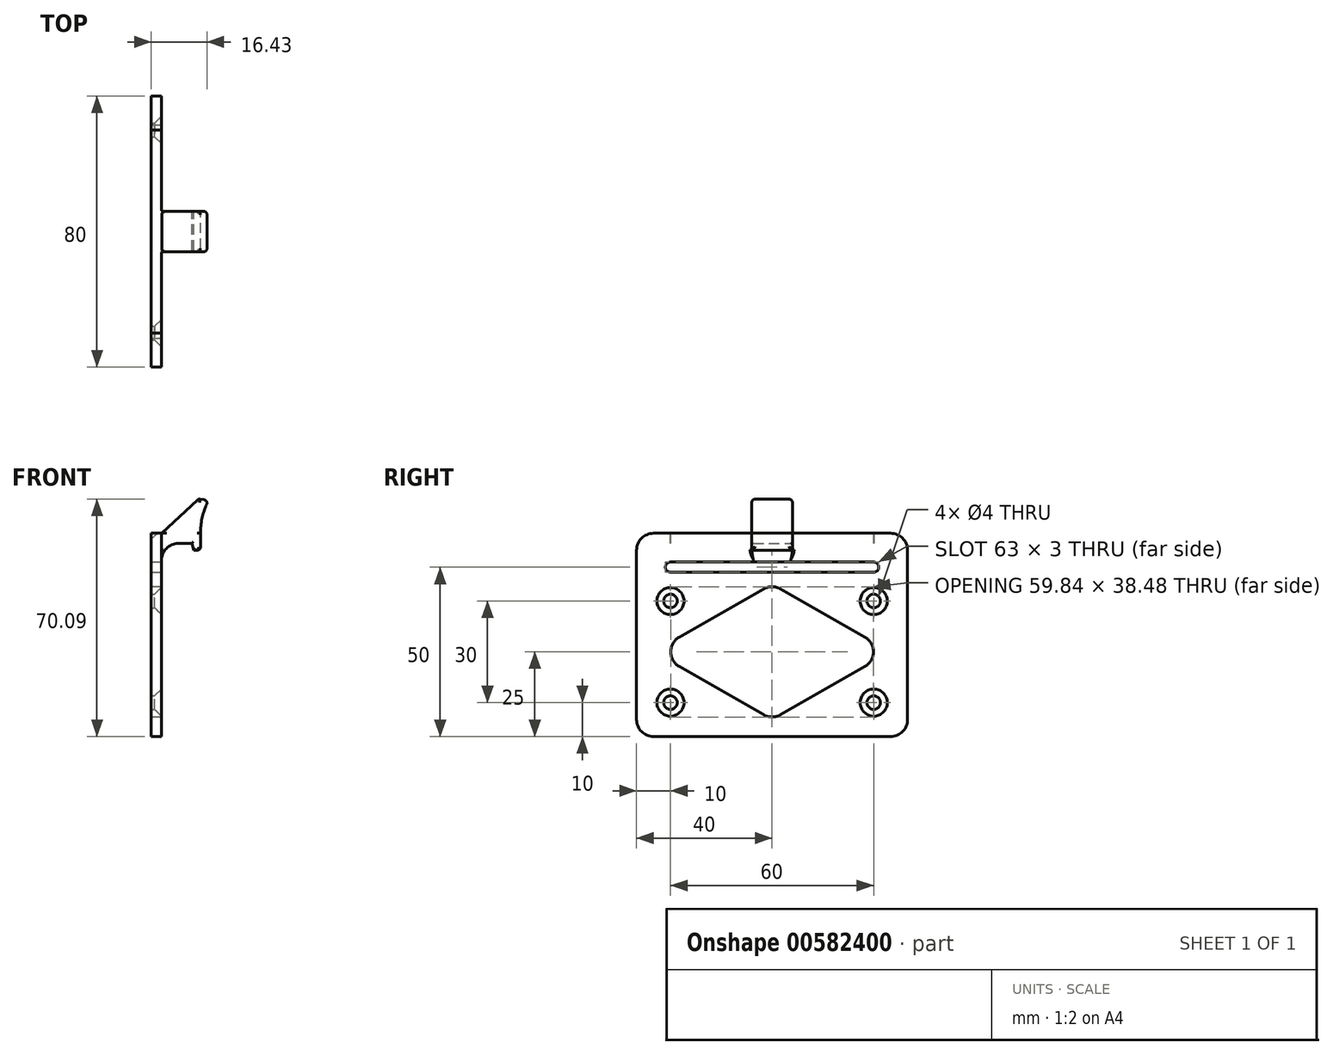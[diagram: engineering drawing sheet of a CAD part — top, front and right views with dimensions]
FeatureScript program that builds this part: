
annotation { "Feature Type Name" : "Feature", "Feature Type Description" : "" }
export const myFeature = defineFeature(function(context is Context, id is Id, definition is map)
    precondition{}
    {
        {
            var Q0;
            Q0=qCreatedBy(makeId("Front.planeOp"),FACE);
            var sketch = newSketch(context, id + "F0", { "sketchPlane" : qUnion([Q0])});
            skLineSegment(sketch, "E0.bottom", {"start": v(0, 0) * mm, "end": v(3, 0) * mm});
            skLineSegment(sketch, "E0.top", {"start": v(0, 60) * mm, "end": v(14.54, 60) * mm});
            skLineSegment(sketch, "E0.left", {"start": v(0, 0) * mm, "end": v(0, 60) * mm});
            skLineSegment(sketch, "E0.right", {"start": v(14.54, 55) * mm, "end": v(14.54, 60) * mm});
            skLineSegment(sketch, "E1", {"start": v(14.54, 55) * mm, "end": v(12.54, 55) * mm});
            skLineSegment(sketch, "E2", {"start": v(3, 52) * mm, "end": v(3, 0) * mm});
            skLineSegment(sketch, "E3", {"start": v(8, 57) * mm, "end": v(12, 57) * mm});
            skPoint(sketch, "E4.newPointA", {"position": v(3, 55) * mm});
            skArc(sketch, "E4.filletArc", {"start": v(8, 57) * mm, "mid": v(4.46, 55.54) * mm, "end": v(3, 52) * mm});
            skLineSegment(sketch, "E5", {"start": v(12, 57) * mm, "end": v(12.54, 55) * mm});
            skPoint(sketch, "E6.orphan", {"position": v(10.1, 55) * mm});
            skSolve(sketch);
        }
        {
            var Q0;
            Q0=makeQuery(id+"F0.imprint","IMPRINT",FACE,{"disambiguationData":[TD([[makeQuery(id+"F0.imprint","IMPRINT",EDGE,{"derivedFrom":sQuery(id+"F0.wireOp",EDGE,"E0.bottom")}),1.0]])]});
            extrude(context, id + "F1", {"entities" : qUnion([Q0]), "endBound" : BoundingType.SYMMETRIC, "depth" : 80 * mm, "offsetDistance" : 25 * mm});
        }
        {
            var Q0;
            Q0=makeQuery(id+"F1.opExtrude","SWEPT_FACE",FACE,{"disambiguationData":[OSD([sQuery(id+"F0.wireOp",EDGE,"E0.top")])]});
            var sketch = newSketch(context, id + "F2", { "sketchPlane" : qUnion([Q0])});
            skLineSegment(sketch, "E7", {"start": v(3, -40) * mm, "end": v(3, -6) * mm});
            skLineSegment(sketch, "E8", {"start": v(3, -6) * mm, "end": v(14.54, -6) * mm});
            skLineSegment(sketch, "E9.MirrorCS", {"start": v(3, 6) * mm, "end": v(14.54, 6) * mm});
            skLineSegment(sketch, "E10.MirrorCS", {"start": v(3, 40) * mm, "end": v(3, 6) * mm});
            skSolve(sketch);
        }
        {
            var Q0;
            {var subQ0=sQuery(id+"F2.wireOp",EDGE,"E7");Q0=makeQuery(id+"F2.imprint","IMPRINT",FACE,{"disambiguationData":[TD([[makeQuery(id+"F2.imprint","IMPRINT",EDGE,{"derivedFrom":subQ0}),-1.0]])]});}
            var Q1;
            {var subQ0=sQuery(id+"F2.wireOp",EDGE,"E9.MirrorCS");Q1=makeQuery(id+"F2.imprint","IMPRINT",FACE,{"disambiguationData":[TD([[makeQuery(id+"F2.imprint","IMPRINT",EDGE,{"derivedFrom":subQ0}),1.0]])]});}
            extrude(context, id + "F3", {"entities" : qUnion([Q0, Q1]), "operationType" : NewBodyOperationType.REMOVE, "endBound" : BoundingType.THROUGH_ALL, "oppositeDirection" : true, "depth" : 25 * mm, "offsetDistance" : 25 * mm});
        }
        {
            var Q0;
            Q0=makeQuery(id+"F3.boolean.opBoolean","MERGE",FACE,{"derivedFrom":[makeQuery(id+"F1.opExtrude","SWEPT_FACE",FACE,{"disambiguationData":[OSD([sQuery(id+"F0.wireOp",EDGE,"E2")])]}),makeQuery(id+"F3.opExtrude","SWEPT_FACE",FACE,{"disambiguationData":[OSD([sQuery(id+"F2.wireOp",EDGE,"E7")])]}),makeQuery(id+"F3.opExtrude","SWEPT_FACE",FACE,{"disambiguationData":[OSD([sQuery(id+"F2.wireOp",EDGE,"E10.MirrorCS")])]})]});
            var sketch = newSketch(context, id + "F4", { "sketchPlane" : qUnion([Q0])});
            skLineSegment(sketch, "E11.bottom", {"start": v(-30, 51.5) * mm, "end": v(30, 51.5) * mm});
            skLineSegment(sketch, "E11.top", {"start": v(-30, 48.5) * mm, "end": v(30, 48.5) * mm});
            skArc(sketch, "E12", {"start": v(30, 48.5) * mm, "mid": v(31.5, 50) * mm, "end": v(30, 51.5) * mm});
            skArc(sketch, "E13", {"start": v(-30, 51.5) * mm, "mid": v(-31.5, 50) * mm, "end": v(-30, 48.5) * mm});
            skSolve(sketch);
        }
        {
            var Q0;
            Q0=makeQuery(id+"F4.imprint","IMPRINT",FACE,{"disambiguationData":[TD([[makeQuery(id+"F4.imprint","IMPRINT",EDGE,{"derivedFrom":sQuery(id+"F4.wireOp",EDGE,"E11.bottom")}),-1.0]])]});
            extrude(context, id + "F5", {"entities" : qUnion([Q0]), "operationType" : NewBodyOperationType.REMOVE, "endBound" : BoundingType.THROUGH_ALL, "oppositeDirection" : true, "depth" : 25 * mm, "offsetDistance" : 25 * mm});
        }
        {
            var Q0;
            Q0=qCreatedBy(makeId("Front.planeOp"),FACE);
            var sketch = newSketch(context, id + "F6", { "sketchPlane" : qUnion([Q0])});
            skArc(sketch, "E14", {"start": v(3, 60) * mm, "mid": v(0.88, 59.12) * mm, "end": v(0, 57) * mm});
            skLineSegment(sketch, "E15", {"start": v(0, 57) * mm, "end": v(0, 60) * mm});
            skLineSegment(sketch, "E16", {"start": v(0, 60) * mm, "end": v(3, 60) * mm});
            skSolve(sketch);
        }
        {
            var Q0;
            Q0 = qSketchRegion(id + "F6", true);
            extrude(context, id + "F7", {"entities" : qUnion([Q0]), "operationType" : NewBodyOperationType.REMOVE, "endBound" : BoundingType.SYMMETRIC, "depth" : 60 * mm, "offsetDistance" : 25 * mm});
        }
        {
            var Q0;
            Q0=qCreatedBy(makeId("Front.planeOp"),FACE);
            var sketch = newSketch(context, id + "F8", { "sketchPlane" : qUnion([Q0])});
            skArc(sketch, "E17", {"start": v(16.94, 69.7) * mm, "mid": v(15.12, 65) * mm, "end": v(14.54, 60) * mm});
            skLineSegment(sketch, "E18", {"start": v(3, 59.92) * mm, "end": v(13.97, 70.15) * mm});
            skLineSegment(sketch, "E19", {"start": v(13.97, 70.15) * mm, "end": v(16.94, 69.7) * mm});
            skLineSegment(sketch, "E20", {"start": v(14.54, 60) * mm, "end": v(3.08, 60) * mm});
            skSolve(sketch);
        }
        {
            var Q0;
            Q0 = qSketchRegion(id + "F8", true);
            extrude(context, id + "F9", {"entities" : qUnion([Q0]), "operationType" : NewBodyOperationType.ADD, "endBound" : BoundingType.SYMMETRIC, "depth" : 12 * mm, "offsetDistance" : 25 * mm});
        }
        {
            var Q0;
            Q0=makeQuery(id+"F1.opExtrude","CAP_EDGE",EDGE,{"disambiguationData":[OSD([sQuery(id+"F0.wireOp",EDGE,"E0.bottom")])],"isStart":true});
            var Q1;
            Q1=makeQuery(id+"F1.opExtrude","CAP_EDGE",EDGE,{"disambiguationData":[OSD([sQuery(id+"F0.wireOp",EDGE,"E0.top")])],"isStart":true});
            var Q2;
            Q2=makeQuery(id+"F1.opExtrude","CAP_EDGE",EDGE,{"disambiguationData":[OSD([sQuery(id+"F0.wireOp",EDGE,"E0.top")])],"isStart":false});
            var Q3;
            Q3=makeQuery(id+"F1.opExtrude","CAP_EDGE",EDGE,{"disambiguationData":[OSD([sQuery(id+"F0.wireOp",EDGE,"E0.bottom")])],"isStart":false});
            fillet(context, id + "F10", {"entities" : qUnion([Q0, Q1, Q2, Q3]), "radius" : 5 * mm, "tangentPropagation" : true, "allowEdgeOverflow" : false});
        }
        {
            var Q0;
            Q0=makeQuery(id+"F3.boolean.opBoolean","COPY",EDGE,{"derivedFrom":makeQuery(id+"F3.opExtrude","SWEPT_EDGE",EDGE,{"disambiguationData":[OSD([sQuery(id+"F2.wireOp",EDGE,"E7"),sQuery(id+"F2.wireOp",EDGE,"E8")])]})});
            var Q1;
            Q1=makeQuery(id+"F3.boolean.opBoolean","INTERSECT",EDGE,{"derivedFrom":[makeQuery(id+"F1.opExtrude","SWEPT_FACE",FACE,{"disambiguationData":[OSD([sQuery(id+"F0.wireOp",EDGE,"E1")])]}),makeQuery(id+"F3.opExtrude","SWEPT_FACE",FACE,{"disambiguationData":[OSD([sQuery(id+"F2.wireOp",EDGE,"E8")])]})]});
            var Q2;
            Q2=makeQuery(id+"F3.boolean.opBoolean","INTERSECT",EDGE,{"derivedFrom":[makeQuery(id+"F1.opExtrude","SWEPT_FACE",FACE,{"disambiguationData":[OSD([sQuery(id+"F0.wireOp",EDGE,"E5")])]}),makeQuery(id+"F3.opExtrude","SWEPT_FACE",FACE,{"disambiguationData":[OSD([sQuery(id+"F2.wireOp",EDGE,"E8")])]})]});
            var Q3;
            Q3=makeQuery(id+"F3.boolean.opBoolean","INTERSECT",EDGE,{"derivedFrom":[makeQuery(id+"F1.opExtrude","SWEPT_FACE",FACE,{"disambiguationData":[OSD([sQuery(id+"F0.wireOp",EDGE,"E3")])]}),makeQuery(id+"F3.opExtrude","SWEPT_FACE",FACE,{"disambiguationData":[OSD([sQuery(id+"F2.wireOp",EDGE,"E8")])]})]});
            var Q4;
            Q4=makeQuery(id+"F3.boolean.opBoolean","INTERSECT",EDGE,{"derivedFrom":[makeQuery(id+"F1.opExtrude","SWEPT_FACE",FACE,{"disambiguationData":[OSD([sQuery(id+"F0.wireOp",EDGE,"E4.filletArc")])]}),makeQuery(id+"F3.opExtrude","SWEPT_FACE",FACE,{"disambiguationData":[OSD([sQuery(id+"F2.wireOp",EDGE,"E8")])]})]});
            fillet(context, id + "F11", {"entities" : qUnion([Q0, Q1, Q2, Q3, Q4]), "radius" : .5 * mm, "tangentPropagation" : true, "allowEdgeOverflow" : false});
        }
        {
            var Q0;
            Q0=makeQuery(id+"F3.boolean.opBoolean","COPY",EDGE,{"derivedFrom":makeQuery(id+"F3.opExtrude","SWEPT_EDGE",EDGE,{"disambiguationData":[OSD([sQuery(id+"F2.wireOp",EDGE,"E9.MirrorCS"),sQuery(id+"F2.wireOp",EDGE,"E10.MirrorCS")])]})});
            var Q1;
            Q1=makeQuery(id+"F3.boolean.opBoolean","INTERSECT",EDGE,{"derivedFrom":[makeQuery(id+"F1.opExtrude","SWEPT_FACE",FACE,{"disambiguationData":[OSD([sQuery(id+"F0.wireOp",EDGE,"E4.filletArc")])]}),makeQuery(id+"F3.opExtrude","SWEPT_FACE",FACE,{"disambiguationData":[OSD([sQuery(id+"F2.wireOp",EDGE,"E9.MirrorCS")])]})]});
            var Q2;
            Q2=makeQuery(id+"F3.boolean.opBoolean","INTERSECT",EDGE,{"derivedFrom":[makeQuery(id+"F1.opExtrude","SWEPT_FACE",FACE,{"disambiguationData":[OSD([sQuery(id+"F0.wireOp",EDGE,"E3")])]}),makeQuery(id+"F3.opExtrude","SWEPT_FACE",FACE,{"disambiguationData":[OSD([sQuery(id+"F2.wireOp",EDGE,"E9.MirrorCS")])]})]});
            var Q3;
            Q3=makeQuery(id+"F3.boolean.opBoolean","INTERSECT",EDGE,{"derivedFrom":[makeQuery(id+"F1.opExtrude","SWEPT_FACE",FACE,{"disambiguationData":[OSD([sQuery(id+"F0.wireOp",EDGE,"E5")])]}),makeQuery(id+"F3.opExtrude","SWEPT_FACE",FACE,{"disambiguationData":[OSD([sQuery(id+"F2.wireOp",EDGE,"E9.MirrorCS")])]})]});
            var Q4;
            Q4=makeQuery(id+"F3.boolean.opBoolean","INTERSECT",EDGE,{"derivedFrom":[makeQuery(id+"F1.opExtrude","SWEPT_FACE",FACE,{"disambiguationData":[OSD([sQuery(id+"F0.wireOp",EDGE,"E1")])]}),makeQuery(id+"F3.opExtrude","SWEPT_FACE",FACE,{"disambiguationData":[OSD([sQuery(id+"F2.wireOp",EDGE,"E9.MirrorCS")])]})]});
            fillet(context, id + "F12", {"entities" : qUnion([Q0, Q1, Q2, Q3, Q4]), "radius" : .5 * mm, "tangentPropagation" : true, "allowEdgeOverflow" : false});
        }
        {
            var Q0;
            Q0=makeQuery(id+"F3.boolean.opBoolean","COPY",EDGE,{"derivedFrom":makeQuery(id+"F3.opExtrude","SWEPT_EDGE",EDGE,{"disambiguationData":[OSD([sQuery(id+"F0.wireOp",EDGE,"E0.top"),sQuery(id+"F0.wireOp",EDGE,"E0.right"),sQuery(id+"F2.wireOp",EDGE,"E8")])]})});
            var Q1;
            Q1=makeQuery(id+"F11.opFillet","BLEND_EDGE",EDGE,{"blendedFrom":[makeQuery(id+"F3.boolean.opBoolean","INTERSECT",EDGE,{"derivedFrom":[makeQuery(id+"F1.opExtrude","SWEPT_FACE",FACE,{"disambiguationData":[OSD([sQuery(id+"F0.wireOp",EDGE,"E1")])]}),makeQuery(id+"F3.opExtrude","SWEPT_FACE",FACE,{"disambiguationData":[OSD([sQuery(id+"F2.wireOp",EDGE,"E8")])]})]}),makeQuery(id+"F1.opExtrude","SWEPT_FACE",FACE,{"disambiguationData":[OSD([sQuery(id+"F0.wireOp",EDGE,"E0.right")])]})],"blendedInto":[makeQuery(id+"F1.opExtrude","SWEPT_FACE",FACE,{"disambiguationData":[OSD([sQuery(id+"F0.wireOp",EDGE,"E0.right")])]})]});
            var Q2;
            Q2=makeQuery(id+"F1.opExtrude","SWEPT_EDGE",EDGE,{"disambiguationData":[OSD([sQuery(id+"F0.wireOp",EDGE,"E0.right"),sQuery(id+"F0.wireOp",EDGE,"E1")])]});
            var Q3;
            Q3=makeQuery(id+"F12.opFillet","BLEND_EDGE",EDGE,{"blendedFrom":[makeQuery(id+"F3.boolean.opBoolean","INTERSECT",EDGE,{"derivedFrom":[makeQuery(id+"F1.opExtrude","SWEPT_FACE",FACE,{"disambiguationData":[OSD([sQuery(id+"F0.wireOp",EDGE,"E1")])]}),makeQuery(id+"F3.opExtrude","SWEPT_FACE",FACE,{"disambiguationData":[OSD([sQuery(id+"F2.wireOp",EDGE,"E9.MirrorCS")])]})]}),makeQuery(id+"F1.opExtrude","SWEPT_FACE",FACE,{"disambiguationData":[OSD([sQuery(id+"F0.wireOp",EDGE,"E0.right")])]})],"blendedInto":[makeQuery(id+"F1.opExtrude","SWEPT_FACE",FACE,{"disambiguationData":[OSD([sQuery(id+"F0.wireOp",EDGE,"E0.right")])]})]});
            var Q4;
            Q4=makeQuery(id+"F3.boolean.opBoolean","COPY",EDGE,{"derivedFrom":makeQuery(id+"F3.opExtrude","SWEPT_EDGE",EDGE,{"disambiguationData":[OSD([sQuery(id+"F0.wireOp",EDGE,"E0.top"),sQuery(id+"F0.wireOp",EDGE,"E0.right"),sQuery(id+"F2.wireOp",EDGE,"E9.MirrorCS")])]})});
            var Q5;
            Q5=makeQuery(id+"F9.opExtrude","CAP_EDGE",EDGE,{"disambiguationData":[OSD([sQuery(id+"F8.wireOp",EDGE,"E19")])],"isStart":true});
            var Q6;
            Q6=makeQuery(id+"F9.opExtrude","CAP_EDGE",EDGE,{"disambiguationData":[OSD([sQuery(id+"F8.wireOp",EDGE,"E19")])],"isStart":false});
            fillet(context, id + "F13", {"entities" : qUnion([Q0, Q1, Q2, Q3, Q4, Q5, Q6]), "radius" : 1 * mm, "tangentPropagation" : true, "allowEdgeOverflow" : false});
        }
        {
            var Q0;
            Q0=makeQuery(id+"F9.opExtrude","CAP_EDGE",EDGE,{"disambiguationData":[OSD([sQuery(id+"F8.wireOp",EDGE,"E17")])],"isStart":false});
            fillet(context, id + "F14", {"entities" : qUnion([Q0]), "radius" : 1 * mm, "tangentPropagation" : true, "allowEdgeOverflow" : false});
        }
        {
            var Q0;
            Q0=makeQuery(id+"F9.opExtrude","CAP_EDGE",EDGE,{"disambiguationData":[OSD([sQuery(id+"F8.wireOp",EDGE,"E18")])],"isStart":false});
            var Q1;
            Q1=makeQuery(id+"F13.opFillet","BLEND_EDGE",EDGE,{"blendedFrom":[makeQuery(id+"F9.opExtrude","CAP_EDGE",EDGE,{"disambiguationData":[OSD([sQuery(id+"F8.wireOp",EDGE,"E19")])],"isStart":false}),makeQuery(id+"F9.opExtrude","SWEPT_FACE",FACE,{"disambiguationData":[OSD([sQuery(id+"F8.wireOp",EDGE,"E18")])]})],"blendedInto":[makeQuery(id+"F9.opExtrude","SWEPT_FACE",FACE,{"disambiguationData":[OSD([sQuery(id+"F8.wireOp",EDGE,"E18")])]})]});
            fillet(context, id + "F15", {"entities" : qUnion([Q0, Q1]), "radius" : 1 * mm, "tangentPropagation" : true, "allowEdgeOverflow" : false});
        }
        {
            var Q0;
            Q0=makeQuery(id+"F3.boolean.opBoolean","MERGE",FACE,{"derivedFrom":[makeQuery(id+"F1.opExtrude","SWEPT_FACE",FACE,{"disambiguationData":[OSD([sQuery(id+"F0.wireOp",EDGE,"E2")])]}),makeQuery(id+"F3.opExtrude","SWEPT_FACE",FACE,{"disambiguationData":[OSD([sQuery(id+"F2.wireOp",EDGE,"E7")])]}),makeQuery(id+"F3.opExtrude","SWEPT_FACE",FACE,{"disambiguationData":[OSD([sQuery(id+"F2.wireOp",EDGE,"E10.MirrorCS")])]})]});
            var sketch = newSketch(context, id + "F16", { "sketchPlane" : qUnion([Q0])});
            skPoint(sketch, "E21", {"position": v(30, 40) * mm});
            skPoint(sketch, "E22", {"position": v(-30, 40) * mm});
            skPoint(sketch, "E23", {"position": v(30, 10) * mm});
            skPoint(sketch, "E24", {"position": v(-30, 10) * mm});
            skSolve(sketch);
        }
        {
            var Q0;
            Q0=sQuery(id+"F16.wireOp",VERTEX,"E22");
            var Q1;
            Q1=sQuery(id+"F16.wireOp",VERTEX,"E21");
            var Q2;
            Q2=sQuery(id+"F16.wireOp",VERTEX,"E24");
            var Q3;
            Q3=sQuery(id+"F16.wireOp",VERTEX,"E23");
            var Q4;
            Q4=makeQuery(id+"F1.opExtrude","SWEPT_BODY",BODY,{"disambiguationData":[OSD([sQuery(id+"F0.wireOp",EDGE,"E0.bottom"),sQuery(id+"F0.wireOp",EDGE,"E0.top"),sQuery(id+"F0.wireOp",EDGE,"E0.left"),sQuery(id+"F0.wireOp",EDGE,"E0.right"),sQuery(id+"F0.wireOp",EDGE,"E1"),sQuery(id+"F0.wireOp",EDGE,"E2"),sQuery(id+"F0.wireOp",EDGE,"E3"),sQuery(id+"F0.wireOp",EDGE,"E4.filletArc"),sQuery(id+"F0.wireOp",EDGE,"E5")])]});
            hole(context, id + "F17", {"style" : HoleStyle.C_SINK, "endStyle" : HoleEndStyle.THROUGH, "holeDiameter" : 4 * mm, "cSinkDiameter" : 8 * mm, "cSinkAngle" : 90 * degree, "majorDiameter" : 5 * mm, "isTappedThrough" : true, "tappedDepth" : 12 * mm, "tapClearance" : 3, "startFromSketch" : true, "locations" : qUnion([Q0, Q1, Q2, Q3]), "scope" : qUnion([Q4])});
        }
        {
            var Q0;
            Q0=qCreatedBy(makeId("Right.planeOp"),FACE);
            var sketch = newSketch(context, id + "F18", { "sketchPlane" : qUnion([Q0])});
            skLineSegment(sketch, "E25", {"start": v(-2.48, 6.42) * mm, "end": v(-27.4, 20.66) * mm});
            skLineSegment(sketch, "E26", {"start": v(-27.4, 29.34) * mm, "end": v(-2.48, 43.58) * mm});
            skLineSegment(sketch, "E27", {"start": v(2.48, 43.58) * mm, "end": v(27.4, 29.34) * mm});
            skLineSegment(sketch, "E28", {"start": v(27.4, 20.66) * mm, "end": v(2.48, 6.42) * mm});
            skPoint(sketch, "E29.visualSharp", {"position": v(-35, 25) * mm});
            skArc(sketch, "E29.filletArc", {"start": v(-27.4, 29.34) * mm, "mid": v(-29.92, 25) * mm, "end": v(-27.4, 20.66) * mm});
            skPoint(sketch, "E30.visualSharp", {"position": v(35, 25) * mm});
            skArc(sketch, "E30.filletArc", {"start": v(27.4, 20.66) * mm, "mid": v(29.92, 25) * mm, "end": v(27.4, 29.34) * mm});
            skPoint(sketch, "E31.visualSharp", {"position": v(0, 5) * mm});
            skArc(sketch, "E31.filletArc", {"start": v(-2.48, 6.42) * mm, "mid": v(0, 5.76) * mm, "end": v(2.48, 6.42) * mm});
            skPoint(sketch, "E32.visualSharp", {"position": v(0, 45) * mm});
            skArc(sketch, "E32.filletArc", {"start": v(2.48, 43.58) * mm, "mid": v(0, 44.24) * mm, "end": v(-2.48, 43.58) * mm});
            skSolve(sketch);
        }
        {
            var Q0;
            Q0=makeQuery(id+"F18.imprint","IMPRINT",FACE,{"disambiguationData":[TD([[makeQuery(id+"F18.imprint","IMPRINT",EDGE,{"derivedFrom":sQuery(id+"F18.wireOp",EDGE,"E25")}),-1.0]])]});
            extrude(context, id + "F19", {"entities" : qUnion([Q0]), "operationType" : NewBodyOperationType.REMOVE, "endBound" : BoundingType.THROUGH_ALL, "depth" : 25 * mm, "offsetDistance" : 25 * mm});
        }
    });
